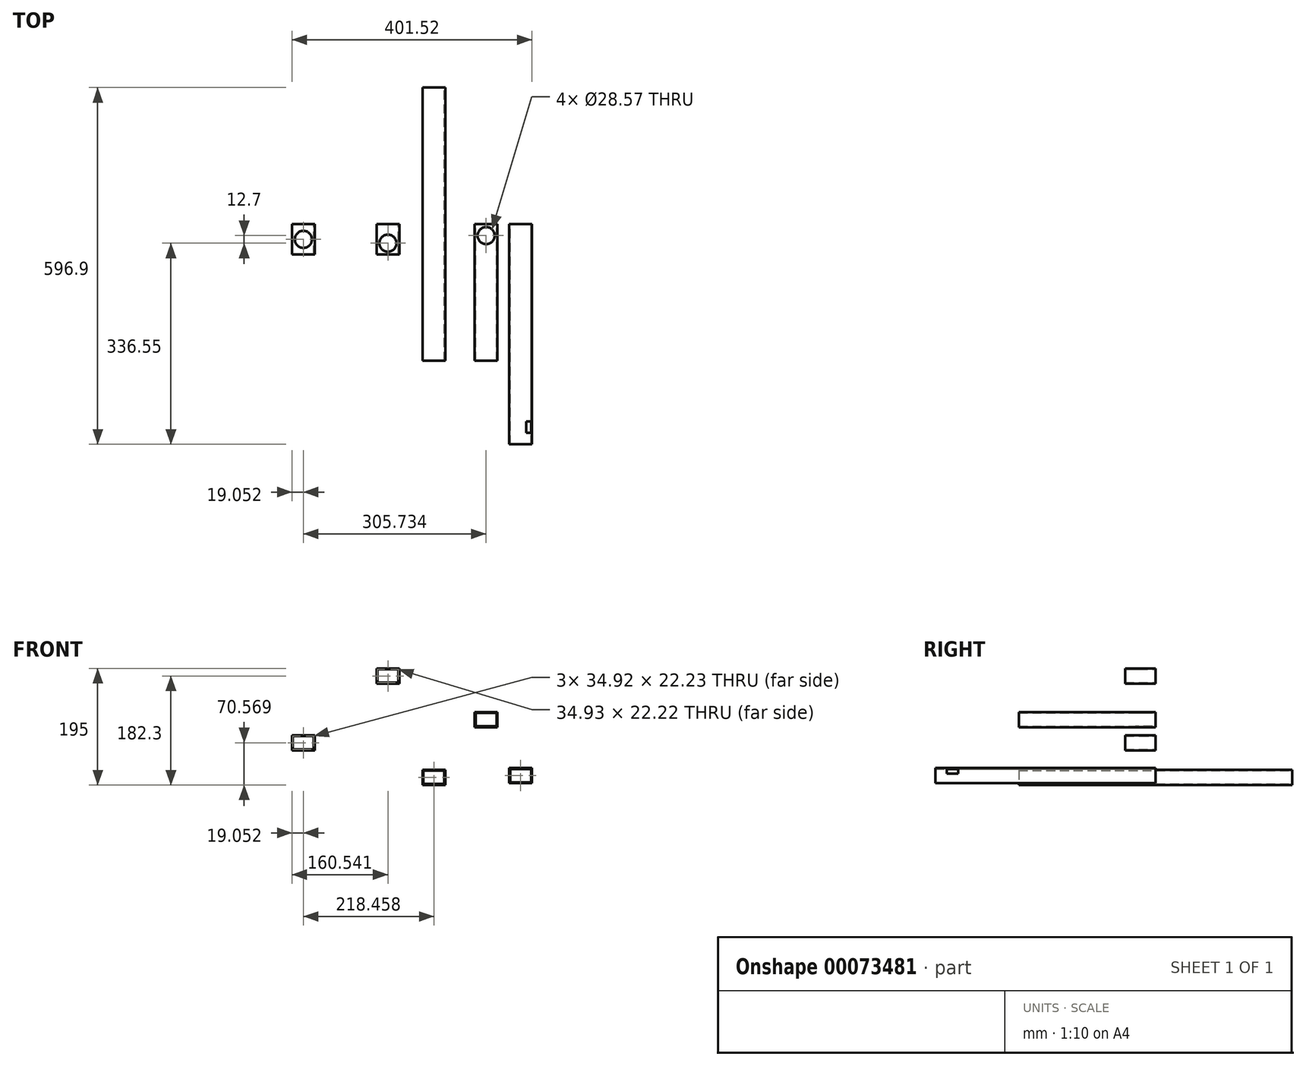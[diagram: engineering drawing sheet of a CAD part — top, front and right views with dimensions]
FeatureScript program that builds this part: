
annotation { "Feature Type Name" : "Feature", "Feature Type Description" : "" }
export const myFeature = defineFeature(function(context is Context, id is Id, definition is map)
    precondition{}
    {
        {
            var Q0;
            Q0=qCreatedBy(makeId("Front.planeOp"),FACE);
            var sketch = newSketch(context, id + "F0", { "sketchPlane" : qUnion([Q0])});
            skLineSegment(sketch, "E0.rect.bottom", {"start": v(17.46, 11.11) * mm, "end": v(-17.46, 11.11) * mm});
            skLineSegment(sketch, "E0.rect.top", {"start": v(17.46, -11.11) * mm, "end": v(-17.46, -11.11) * mm});
            skLineSegment(sketch, "E0.rect.left", {"start": v(17.46, 11.11) * mm, "end": v(17.46, -11.11) * mm});
            skLineSegment(sketch, "E0.rect.right", {"start": v(-17.46, 11.11) * mm, "end": v(-17.46, -11.11) * mm});
            skPoint(sketch, "E0.rect.middle", {"position": v(0, 0) * mm});
            skLineSegment(sketch, "E1.0", {"start": v(19.05, 12.7) * mm, "end": v(-19.05, 12.7) * mm});
            skLineSegment(sketch, "E1.1", {"start": v(19.05, 12.7) * mm, "end": v(19.05, -12.7) * mm});
            skLineSegment(sketch, "E1.2", {"start": v(19.05, -12.7) * mm, "end": v(-19.05, -12.7) * mm});
            skLineSegment(sketch, "E1.3", {"start": v(-19.05, 12.7) * mm, "end": v(-19.05, -12.7) * mm});
            skSolve(sketch);
        }
        {
            var Q0;
            Q0=qSketchRegion(id+"F0",true);
            extrude(context, id + "F1", {"entities" : qUnion([Q0]), "endBound" : BoundingType.SYMMETRIC, "depth" : 457.2 * mm});
        }
        {
            var Q0;
            Q0=qCreatedBy(makeId("Front.planeOp"),FACE);
            var sketch = newSketch(context, id + "F2", { "sketchPlane" : qUnion([Q0])});
            skLineSegment(sketch, "E2.bottom", {"start": v(68.23, 84.01) * mm, "end": v(106.33, 84.01) * mm});
            skLineSegment(sketch, "E2.top", {"start": v(68.23, 109.41) * mm, "end": v(106.33, 109.41) * mm});
            skLineSegment(sketch, "E2.left", {"start": v(68.23, 84.01) * mm, "end": v(68.23, 109.41) * mm});
            skLineSegment(sketch, "E2.right", {"start": v(106.33, 84.01) * mm, "end": v(106.33, 109.41) * mm});
            skLineSegment(sketch, "E3.0", {"start": v(69.81, 107.83) * mm, "end": v(104.74, 107.83) * mm});
            skLineSegment(sketch, "E3.1", {"start": v(69.81, 85.6) * mm, "end": v(69.81, 107.83) * mm});
            skLineSegment(sketch, "E3.2", {"start": v(69.81, 85.6) * mm, "end": v(104.74, 85.6) * mm});
            skLineSegment(sketch, "E3.3", {"start": v(104.74, 85.6) * mm, "end": v(104.74, 107.83) * mm});
            skSolve(sketch);
        }
        {
            var Q0;
            Q0=makeQuery(id+"F2.imprint","IMPRINT",FACE,{"disambiguationData":[TD([[makeQuery(id+"F2.imprint","IMPRINT",EDGE,{"derivedFrom":sQuery(id+"F2.wireOp",EDGE,"E2.bottom")}),1.0]])]});
            extrude(context, id + "F3", {"entities" : qUnion([Q0]), "depth" : 228.6 * mm});
        }
        {
            var Q0;
            Q0=qCreatedBy(makeId("Front.planeOp"),FACE);
            var sketch = newSketch(context, id + "F4", { "sketchPlane" : qUnion([Q0])});
            skLineSegment(sketch, "E4.bottom", {"start": v(-96.02, 156.9) * mm, "end": v(-57.92, 156.9) * mm});
            skLineSegment(sketch, "E4.top", {"start": v(-96.02, 182.3) * mm, "end": v(-57.92, 182.3) * mm});
            skLineSegment(sketch, "E4.left", {"start": v(-96.02, 156.9) * mm, "end": v(-96.02, 182.3) * mm});
            skLineSegment(sketch, "E4.right", {"start": v(-57.92, 156.9) * mm, "end": v(-57.92, 182.3) * mm});
            skLineSegment(sketch, "E5.0", {"start": v(-94.43, 158.49) * mm, "end": v(-59.5, 158.49) * mm});
            skLineSegment(sketch, "E5.1", {"start": v(-94.43, 158.49) * mm, "end": v(-94.43, 180.71) * mm});
            skLineSegment(sketch, "E5.2", {"start": v(-94.43, 180.71) * mm, "end": v(-59.5, 180.71) * mm});
            skLineSegment(sketch, "E5.3", {"start": v(-59.5, 158.49) * mm, "end": v(-59.5, 180.71) * mm});
            skSolve(sketch);
        }
        {
            var Q0;
            Q0=makeQuery(id+"F4.imprint","IMPRINT",FACE,{"disambiguationData":[TD([[makeQuery(id+"F4.imprint","IMPRINT",EDGE,{"derivedFrom":sQuery(id+"F4.wireOp",EDGE,"E4.bottom")}),1.0]])]});
            extrude(context, id + "F5", {"entities" : qUnion([Q0]), "depth" : 50.8 * mm});
        }
        {
            var Q0;
            Q0=qCreatedBy(makeId("Front.planeOp"),FACE);
            var sketch = newSketch(context, id + "F6", { "sketchPlane" : qUnion([Q0])});
            skLineSegment(sketch, "E6.rect.bottom", {"start": v(-201, 68.98) * mm, "end": v(-235.92, 68.98) * mm});
            skLineSegment(sketch, "E6.rect.top", {"start": v(-201, 46.76) * mm, "end": v(-235.92, 46.76) * mm});
            skLineSegment(sketch, "E6.rect.left", {"start": v(-201, 68.98) * mm, "end": v(-201, 46.76) * mm});
            skLineSegment(sketch, "E6.rect.right", {"start": v(-235.92, 68.98) * mm, "end": v(-235.92, 46.76) * mm});
            skPoint(sketch, "E6.rect.middle", {"position": v(-218.46, 57.87) * mm});
            skLineSegment(sketch, "E7.0", {"start": v(-199.4, 70.57) * mm, "end": v(-237.5, 70.57) * mm});
            skLineSegment(sketch, "E7.1", {"start": v(-199.4, 70.57) * mm, "end": v(-199.4, 45.17) * mm});
            skLineSegment(sketch, "E7.2", {"start": v(-199.4, 45.17) * mm, "end": v(-237.5, 45.17) * mm});
            skLineSegment(sketch, "E7.3", {"start": v(-237.5, 70.57) * mm, "end": v(-237.5, 45.17) * mm});
            skSolve(sketch);
        }
        {
            var Q0;
            Q0=makeQuery(id+"F6.imprint","IMPRINT",FACE,{"disambiguationData":[TD([[makeQuery(id+"F6.imprint","IMPRINT",EDGE,{"derivedFrom":sQuery(id+"F6.wireOp",EDGE,"E6.rect.bottom")}),-1.0]])]});
            extrude(context, id + "F7", {"entities" : qUnion([Q0]), "depth" : 50.8 * mm});
        }
        {
            var Q0;
            Q0=makeQuery(id+"F7.opExtrude","SWEPT_FACE",FACE,{"disambiguationData":[OSD([sQuery(id+"F6.wireOp",EDGE,"E7.0")])]});
            var sketch = newSketch(context, id + "F8", { "sketchPlane" : qUnion([Q0])});
            skCircle(sketch, "E8", {"center": v(-218.46, -25.4) * mm, "radius": 14.29 * mm});
            skPoint(sketch, "E8.centerSnap0", {"position": v(-218.46, 0) * mm});
            skPoint(sketch, "E8.centerSnap1", {"position": v(-237.5, -25.4) * mm});
            skSolve(sketch);
        }
        {
            var Q0;
            Q0=qSketchRegion(id+"F8",true);
            extrude(context, id + "F9", {"entities" : qUnion([Q0]), "operationType" : NewBodyOperationType.REMOVE, "endBound" : BoundingType.UP_TO_NEXT, "oppositeDirection" : true, "depth" : 25.4 * mm});
        }
        {
            var Q0;
            Q0=makeQuery(id+"F5.opExtrude","SWEPT_FACE",FACE,{"disambiguationData":[OSD([sQuery(id+"F4.wireOp",EDGE,"E4.top")])]});
            var sketch = newSketch(context, id + "F10", { "sketchPlane" : qUnion([Q0])});
            skCircle(sketch, "E9", {"center": v(-76.97, -31.75) * mm, "radius": 14.29 * mm});
            skSolve(sketch);
        }
        {
            var Q0;
            Q0=makeQuery(id+"F10.imprint","IMPRINT",FACE,{"disambiguationData":[TD([[makeQuery(id+"F10.imprint","IMPRINT",EDGE,{"derivedFrom":sQuery(id+"F10.wireOp",EDGE,"E9")}),1.0]])]});
            extrude(context, id + "F11", {"entities" : qUnion([Q0]), "operationType" : NewBodyOperationType.REMOVE, "oppositeDirection" : true, "depth" : 12.7 * mm});
        }
        {
            var Q0;
            Q0=makeQuery(id+"F3.opExtrude","SWEPT_FACE",FACE,{"disambiguationData":[OSD([sQuery(id+"F2.wireOp",EDGE,"E2.top")])]});
            var sketch = newSketch(context, id + "F12", { "sketchPlane" : qUnion([Q0])});
            skCircle(sketch, "E10", {"center": v(87.28, -19.05) * mm, "radius": 14.29 * mm});
            skPoint(sketch, "E10.centerSnap0", {"position": v(87.28, 0) * mm});
            skSolve(sketch);
        }
        {
            var Q0;
            Q0=makeQuery(id+"F12.imprint","IMPRINT",FACE,{"disambiguationData":[TD([[makeQuery(id+"F12.imprint","IMPRINT",EDGE,{"derivedFrom":sQuery(id+"F12.wireOp",EDGE,"E10")}),1.0]])]});
            extrude(context, id + "F13", {"entities" : qUnion([Q0]), "operationType" : NewBodyOperationType.REMOVE, "endBound" : BoundingType.THROUGH_ALL, "oppositeDirection" : true, "depth" : 25.4 * mm});
        }
        {
            var Q0;
            Q0=qCreatedBy(makeId("Front.planeOp"),FACE);
            var sketch = newSketch(context, id + "F14", { "sketchPlane" : qUnion([Q0])});
            skLineSegment(sketch, "E11.bottom", {"start": v(125.91, -9.77) * mm, "end": v(164.01, -9.77) * mm});
            skLineSegment(sketch, "E11.top", {"start": v(125.91, 15.63) * mm, "end": v(164.01, 15.63) * mm});
            skLineSegment(sketch, "E11.left", {"start": v(125.91, -9.77) * mm, "end": v(125.91, 15.63) * mm});
            skLineSegment(sketch, "E11.right", {"start": v(164.01, -9.77) * mm, "end": v(164.01, 15.63) * mm});
            skLineSegment(sketch, "E12.0", {"start": v(127.5, -8.18) * mm, "end": v(162.43, -8.18) * mm});
            skLineSegment(sketch, "E12.1", {"start": v(127.5, -8.18) * mm, "end": v(127.5, 14.04) * mm});
            skLineSegment(sketch, "E12.2", {"start": v(127.5, 14.04) * mm, "end": v(162.43, 14.04) * mm});
            skLineSegment(sketch, "E12.3", {"start": v(162.43, -8.18) * mm, "end": v(162.43, 14.04) * mm});
            skSolve(sketch);
        }
        {
            var Q0;
            Q0=makeQuery(id+"F14.imprint","IMPRINT",FACE,{"disambiguationData":[TD([[makeQuery(id+"F14.imprint","IMPRINT",EDGE,{"derivedFrom":sQuery(id+"F14.wireOp",EDGE,"E11.bottom")}),1.0]])]});
            extrude(context, id + "F15", {"entities" : qUnion([Q0]), "depth" : 368.3 * mm});
        }
        {
            var Q0;
            Q0=makeQuery(id+"F15.opExtrude","SWEPT_FACE",FACE,{"disambiguationData":[OSD([sQuery(id+"F14.wireOp",EDGE,"E11.right")])]});
            var sketch = newSketch(context, id + "F16", { "sketchPlane" : qUnion([Q0])});
            skLineSegment(sketch, "E13.bottom", {"start": v(-349.25, 6.1) * mm, "end": v(-330.2, 6.1) * mm});
            skLineSegment(sketch, "E13.top", {"start": v(-349.25, 15.63) * mm, "end": v(-330.2, 15.63) * mm});
            skLineSegment(sketch, "E13.left", {"start": v(-349.25, 6.1) * mm, "end": v(-349.25, 15.63) * mm});
            skLineSegment(sketch, "E13.right", {"start": v(-330.2, 6.1) * mm, "end": v(-330.2, 15.63) * mm});
            skSolve(sketch);
        }
        {
            var Q0;
            Q0=makeQuery(id+"F16.imprint","IMPRINT",FACE,{"disambiguationData":[TD([[makeQuery(id+"F16.imprint","IMPRINT",EDGE,{"derivedFrom":sQuery(id+"F16.wireOp",EDGE,"E13.bottom")}),1.0]])]});
            extrude(context, id + "F17", {"entities" : qUnion([Q0]), "operationType" : NewBodyOperationType.REMOVE, "oppositeDirection" : true, "depth" : 9.52 * mm});
        }
    });
